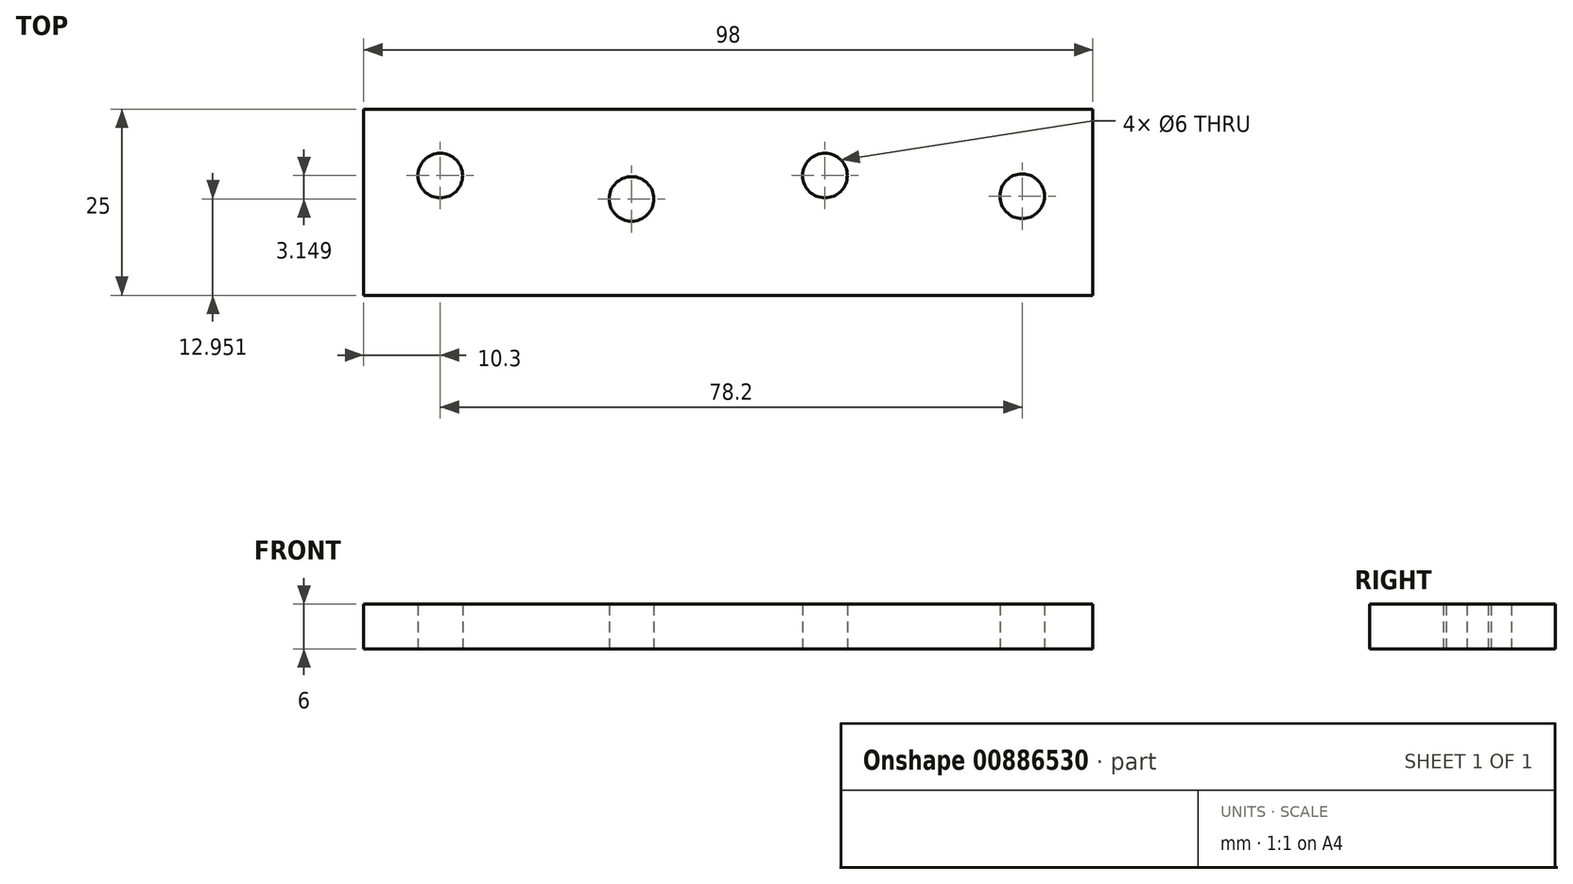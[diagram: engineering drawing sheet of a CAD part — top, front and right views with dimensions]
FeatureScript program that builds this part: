
annotation { "Feature Type Name" : "Feature", "Feature Type Description" : "" }
export const myFeature = defineFeature(function(context is Context, id is Id, definition is map)
    precondition{}
    {
        {
            var Q0;
            Q0=qCreatedBy(makeId("Top.planeOp"),FACE);
            var sketch = newSketch(context, id + "F0", { "sketchPlane" : qUnion([Q0])});
            skLineSegment(sketch, "E0.bottom", {"start": v(-49, -12.5) * mm, "end": v(49, -12.5) * mm});
            skLineSegment(sketch, "E0.top", {"start": v(-49, 12.5) * mm, "end": v(49, 12.5) * mm});
            skLineSegment(sketch, "E0.left", {"start": v(-49, -12.5) * mm, "end": v(-49, 12.5) * mm});
            skLineSegment(sketch, "E0.right", {"start": v(49, -12.5) * mm, "end": v(49, 12.5) * mm});
            skPoint(sketch, "E0.middle", {"position": v(0, 0) * mm});
            skLineSegment(sketch, "E1", {"start": v(-41.66, 12.5) * mm, "end": v(-41.66, 3.6) * mm, "construction": true});
            skLineSegment(sketch, "E2", {"start": v(-49, 3.6) * mm, "end": v(49, 3.6) * mm, "construction": true});
            skLineSegment(sketch, "E3", {"start": v(-44.04, 12.5) * mm, "end": v(-44.04, 0.2) * mm, "construction": true});
            skLineSegment(sketch, "E4", {"start": v(-49, 0.2) * mm, "end": v(49, 0.88) * mm, "construction": true});
            skLineSegment(sketch, "E5", {"start": v(-49, 4.06) * mm, "end": v(-38.7, 4.06) * mm, "construction": true});
            skCircle(sketch, "E6", {"center": v(-38.7, 3.6) * mm, "radius": 3 * mm});
            skLineSegment(sketch, "E7", {"start": v(-49, -0.27) * mm, "end": v(-13, -0.27) * mm, "construction": true});
            skCircle(sketch, "E8", {"center": v(-13, 0.45) * mm, "radius": 3 * mm});
            skLineSegment(sketch, "E9", {"start": v(-49, 6.33) * mm, "end": v(13, 6.9) * mm, "construction": true});
            skCircle(sketch, "E10", {"center": v(13, 3.6) * mm, "radius": 3 * mm});
            skLineSegment(sketch, "E11", {"start": v(-49, -4.76) * mm, "end": v(39.5, -4.76) * mm, "construction": true});
            skCircle(sketch, "E12", {"center": v(39.5, 0.82) * mm, "radius": 3 * mm});
            skSolve(sketch);
        }
        {
            var Q0;
            Q0 = qSketchRegion(id + "F0", true);
            extrude(context, id + "F1", {"entities" : qUnion([Q0]), "depth" : 6 * mm, "offsetDistance" : 25 * mm});
        }
    });
